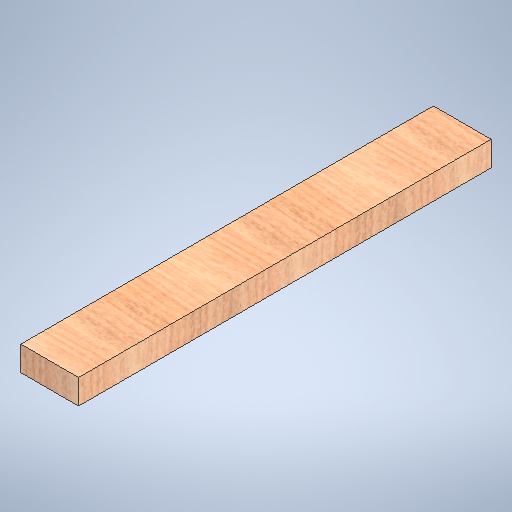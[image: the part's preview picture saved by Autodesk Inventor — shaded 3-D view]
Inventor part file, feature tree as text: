
AUTODESK INVENTOR PART (.ipt)
format: ipt  version: 2025 (Build 290162010, 162A)  size: 338,944 bytes
history: native  units: in
note: dims shown in document units (in); Inventor stores cm internally (conversion verified against a paired STEP export)
features: extrude x1, sketch x1
ambient origin geometry x8: Origin, YZ Plane, XZ Plane, XY Plane, X Axis, Y Axis, Z Axis, Center Point
bodies: Solid1 (feature_tree)
feature tree (2):
  extrude  "Extrusion1"  Depth=1.5in TaperAngle=0.0deg
  sketch  "Sketch1"  dims[d1=3.5in d2=1.5in d3=0.0in d4=25.0in]
